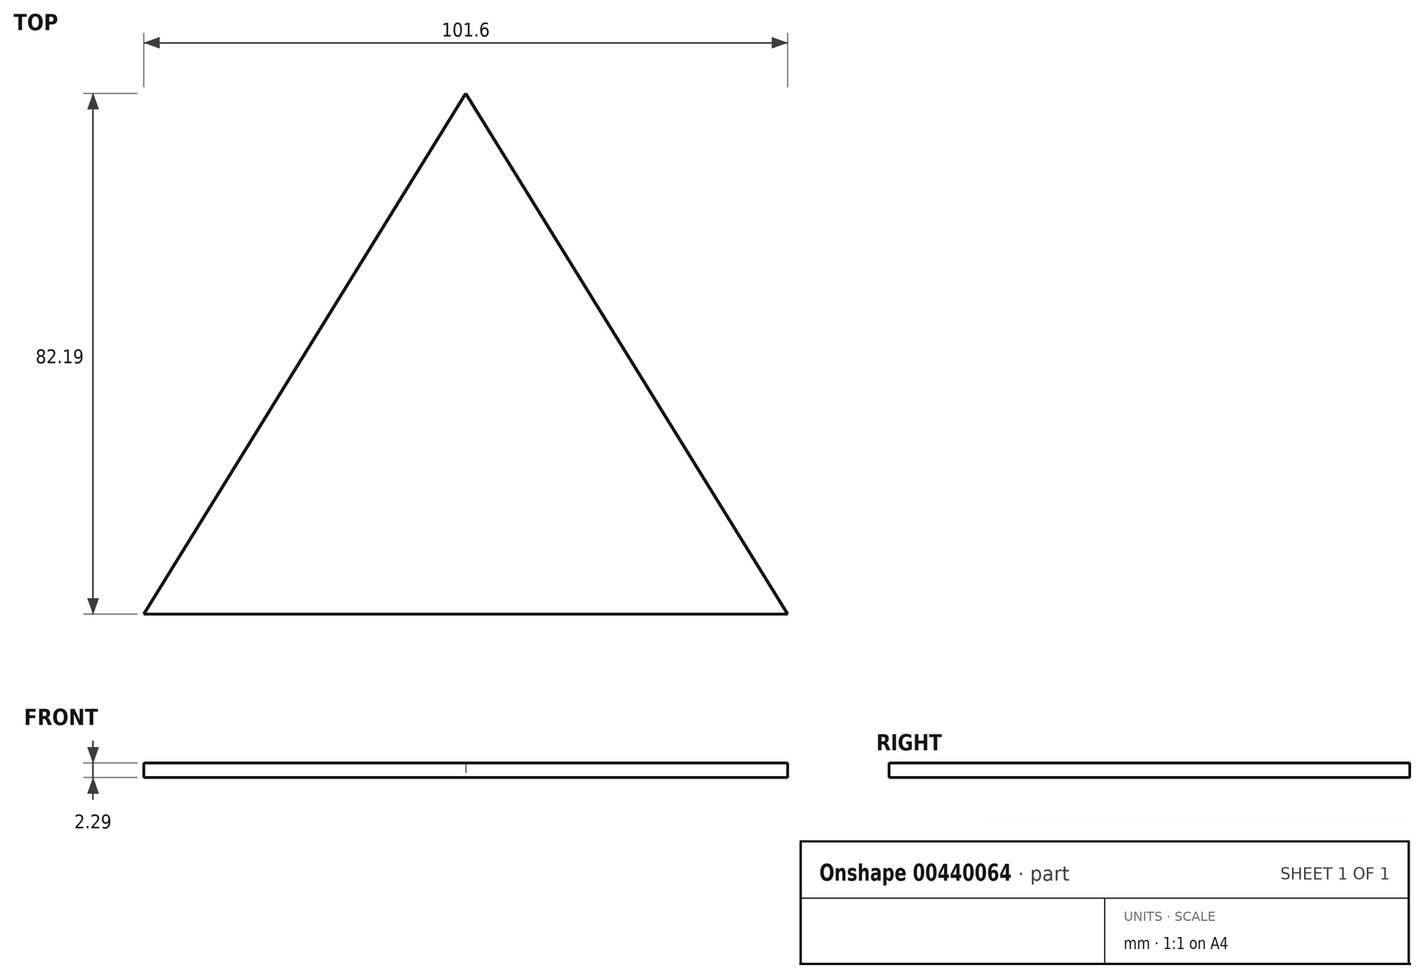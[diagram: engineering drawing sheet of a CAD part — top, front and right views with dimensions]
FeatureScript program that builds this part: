
annotation { "Feature Type Name" : "Feature", "Feature Type Description" : "" }
export const myFeature = defineFeature(function(context is Context, id is Id, definition is map)
    precondition{}
    {
        {
            var Q0;
            Q0=qCreatedBy(makeId("Top.planeOp"),FACE);
            var sketch = newSketch(context, id + "F0", { "sketchPlane" : qUnion([Q0])});
            skLineSegment(sketch, "E0", {"start": v(0, 0) * mm, "end": v(50.8, 0) * mm});
            skLineSegment(sketch, "E1", {"start": v(50.8, 0) * mm, "end": v(0, 82.2) * mm});
            skLineSegment(sketch, "E2.MirrorCS", {"start": v(0, 0) * mm, "end": v(-50.8, 0) * mm});
            skLineSegment(sketch, "E3.MirrorCS", {"start": v(-50.8, 0) * mm, "end": v(0, 82.2) * mm});
            skSolve(sketch);
        }
        {
            var Q0;
            Q0=makeQuery(id+"F0.imprint","IMPRINT",FACE,{"disambiguationData":[TD([[makeQuery(id+"F0.imprint","IMPRINT",EDGE,{"derivedFrom":sQuery(id+"F0.wireOp",EDGE,"E0")}),1.0]])]});
            extrude(context, id + "F1", {"entities" : qUnion([Q0]), "depth" : 2.3 * mm});
        }
    });
